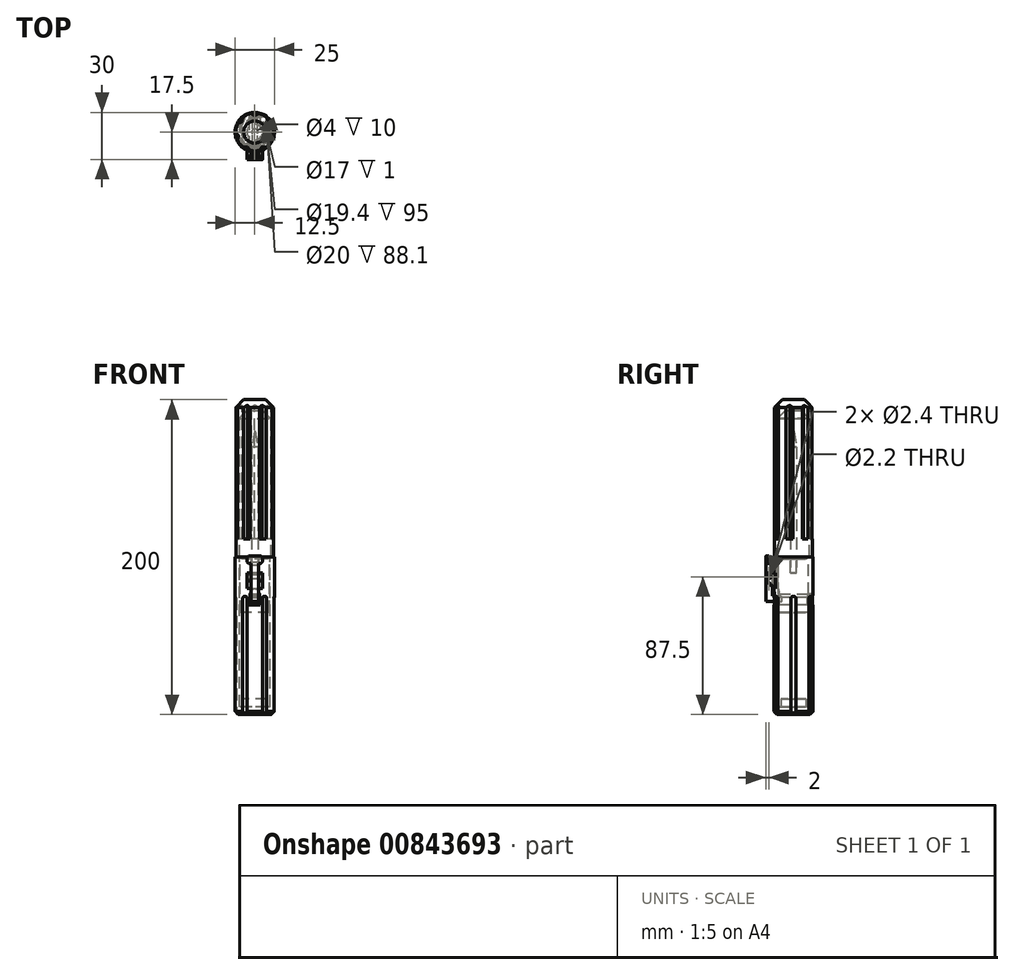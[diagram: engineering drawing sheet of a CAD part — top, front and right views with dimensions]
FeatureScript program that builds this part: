
annotation { "Feature Type Name" : "Feature", "Feature Type Description" : "" }
export const myFeature = defineFeature(function(context is Context, id is Id, definition is map)
    precondition{}
    {
        {
            var Q0;
            Q0=qCreatedBy(makeId("Top.planeOp"),FACE);
            var sketch = newSketch(context, id + "F0", { "sketchPlane" : qUnion([Q0])});
            skCircle(sketch, "E0", {"center": v(0, 0) * mm, "radius": 12.5 * mm});
            skSolve(sketch);
        }
        {
            var Q0;
            Q0=makeQuery(id+"F0.imprint","IMPRINT",FACE,{"disambiguationData":[TD([[makeQuery(id+"F0.imprint","IMPRINT",EDGE,{"derivedFrom":sQuery(id+"F0.wireOp",EDGE,"E0")}),1.0]])]});
            extrude(context, id + "F1", {"entities" : qUnion([Q0]), "depth" : 100 * mm, "offsetDistance" : 25 * mm});
        }
        {
            var Q0;
            Q0=makeQuery(id+"F1.opExtrude","CAP_FACE",FACE,{"disambiguationData":[OSD([sQuery(id+"F0.wireOp",EDGE,"E0")])],"isStart":false});
            var sketch = newSketch(context, id + "F2", { "sketchPlane" : qUnion([Q0])});
            skCircle(sketch, "E1", {"center": v(0, 0) * mm, "radius": 9.7 * mm});
            skSolve(sketch);
        }
        {
            var Q0;
            Q0=qCreatedBy(makeId("Front.planeOp"),FACE);
            var sketch = newSketch(context, id + "F3", { "sketchPlane" : qUnion([Q0])});
            skLineSegment(sketch, "E2.bottom", {"start": v(-5, 85) * mm, "end": v(5, 85) * mm});
            skLineSegment(sketch, "E2.top", {"start": v(-5, 90) * mm, "end": v(5, 90) * mm});
            skLineSegment(sketch, "E2.left", {"start": v(-5, 85) * mm, "end": v(-5, 90) * mm});
            skLineSegment(sketch, "E2.right", {"start": v(5, 85) * mm, "end": v(5, 90) * mm});
            skPoint(sketch, "E2.middle", {"position": v(0, 87.5) * mm});
            skSolve(sketch);
        }
        {
            var Q0;
            Q0 = qSketchRegion(id + "F3", true);
            extrude(context, id + "F4", {"entities" : qUnion([Q0]), "operationType" : NewBodyOperationType.ADD, "depth" : 17.5 * mm, "offsetDistance" : 25 * mm});
        }
        {
            var Q0;
            Q0=makeQuery(id+"F4.boolean.opBoolean","INTERSECT",EDGE,{"derivedFrom":[makeQuery(id+"F1.opExtrude","SWEPT_FACE",FACE,{"disambiguationData":[OSD([sQuery(id+"F0.wireOp",EDGE,"E0")])]}),makeQuery(id+"F4.opExtrude","SWEPT_FACE",FACE,{"disambiguationData":[OSD([sQuery(id+"F3.wireOp",EDGE,"E2.bottom")])]})]});
            chamfer(context, id + "F5", {"entities" : qUnion([Q0]), "width" : 5 * mm, "tangentPropagation" : true});
        }
        {
            var Q0;
            Q0=makeQuery(id+"F4.opExtrude","CAP_FACE",FACE,{"disambiguationData":[OSD([sQuery(id+"F3.wireOp",EDGE,"E2.bottom"),sQuery(id+"F3.wireOp",EDGE,"E2.top"),sQuery(id+"F3.wireOp",EDGE,"E2.left"),sQuery(id+"F3.wireOp",EDGE,"E2.right")])],"isStart":false});
            var sketch = newSketch(context, id + "F6", { "sketchPlane" : qUnion([Q0])});
            skLineSegment(sketch, "E3.bottom", {"start": v(-2.5, 90) * mm, "end": v(2.5, 90) * mm});
            skLineSegment(sketch, "E3.top", {"start": v(-2.5, 80) * mm, "end": v(2.5, 80) * mm});
            skLineSegment(sketch, "E3.left", {"start": v(-2.5, 90) * mm, "end": v(-2.5, 80) * mm});
            skLineSegment(sketch, "E3.right", {"start": v(2.5, 90) * mm, "end": v(2.5, 80) * mm});
            skSolve(sketch);
        }
        {
            var Q0;
            Q0 = qSketchRegion(id + "F6", true);
            extrude(context, id + "F7", {"entities" : qUnion([Q0]), "operationType" : NewBodyOperationType.REMOVE, "oppositeDirection" : true, "depth" : 5 * mm, "offsetDistance" : 25 * mm});
        }
        {
            var Q0;
            {var subQ2=sQuery(id+"F3.wireOp",EDGE,"E2.right");Q0=makeQuery(id+"F4.boolean.opBoolean","SPLIT",FACE,{"disambiguationData":[TD([makeQuery(id+"F1.opExtrude","SWEPT_FACE",FACE,{"disambiguationData":[OSD([sQuery(id+"F0.wireOp",EDGE,"E0")])]})])],"derivedFrom":makeQuery(id+"F4.opExtrude","SWEPT_FACE",FACE,{"disambiguationData":[OSD([subQ2])]})});}
            var sketch = newSketch(context, id + "F8", { "sketchPlane" : qUnion([Q0])});
            skCircle(sketch, "E4", {"center": v(-15.5, 87.5) * mm, "radius": 1.1 * mm});
            skSolve(sketch);
        }
        {
            var Q0;
            Q0 = qSketchRegion(id + "F8", true);
            extrude(context, id + "F9", {"entities" : qUnion([Q0]), "operationType" : NewBodyOperationType.REMOVE, "oppositeDirection" : true, "depth" : 25 * mm, "offsetDistance" : 25 * mm});
        }
        {
            var Q0;
            Q0=makeQuery(id+"F7.boolean.opBoolean","COPY",FACE,{"derivedFrom":makeQuery(id+"F7.opExtrude","CAP_FACE",FACE,{"disambiguationData":[OSD([sQuery(id+"F6.wireOp",EDGE,"E3.bottom"),sQuery(id+"F6.wireOp",EDGE,"E3.top"),sQuery(id+"F6.wireOp",EDGE,"E3.left"),sQuery(id+"F6.wireOp",EDGE,"E3.right")])],"isStart":false})});
            var sketch = newSketch(context, id + "F10", { "sketchPlane" : qUnion([Q0])});
            skLineSegment(sketch, "E5.bottom", {"start": v(-3, 80) * mm, "end": v(3, 80) * mm});
            skLineSegment(sketch, "E5.top", {"start": v(-3, 70) * mm, "end": v(3, 70) * mm});
            skLineSegment(sketch, "E5.left", {"start": v(-3, 80) * mm, "end": v(-3, 70) * mm});
            skLineSegment(sketch, "E5.right", {"start": v(3, 80) * mm, "end": v(3, 70) * mm});
            skSolve(sketch);
        }
        {
            var Q0;
            Q0=makeQuery(id+"F10.imprint","IMPRINT",FACE,{"disambiguationData":[TD([[makeQuery(id+"F10.imprint","IMPRINT",EDGE,{"derivedFrom":sQuery(id+"F10.wireOp",EDGE,"E5.bottom")}),-1.0]])]});
            extrude(context, id + "F11", {"entities" : qUnion([Q0]), "operationType" : NewBodyOperationType.REMOVE, "oppositeDirection" : true, "depth" : 9 * mm, "offsetDistance" : 25 * mm});
        }
        {
            var Q0;
            Q0=makeQuery(id+"F2.imprint","IMPRINT",FACE,{"disambiguationData":[TD([[makeQuery(id+"F2.imprint","IMPRINT",EDGE,{"derivedFrom":sQuery(id+"F2.wireOp",EDGE,"E1")}),1.0]])]});
            extrude(context, id + "F12", {"entities" : qUnion([Q0]), "operationType" : NewBodyOperationType.REMOVE, "oppositeDirection" : true, "depth" : 95 * mm, "offsetDistance" : 25 * mm});
        }
        {
            var Q0;
            Q0=makeQuery(id+"F1.opExtrude","CAP_EDGE",EDGE,{"disambiguationData":[OSD([sQuery(id+"F0.wireOp",EDGE,"E0")])],"isStart":true});
            chamfer(context, id + "F13", {"entities" : qUnion([Q0]), "width" : 2 * mm, "tangentPropagation" : true});
        }
        {
            var Q0;
            Q0=makeQuery(id+"F1.opExtrude","CAP_FACE",FACE,{"disambiguationData":[OSD([sQuery(id+"F0.wireOp",EDGE,"E0")])],"isStart":true});
            var sketch = newSketch(context, id + "F14", { "sketchPlane" : qUnion([Q0])});
            skCircle(sketch, "E6", {"center": v(13.39, 0) * mm, "radius": 1.9 * mm});
            skCircle(sketch, "E7.1.0", {"center": v(6.7, 11.6) * mm, "radius": 1.9 * mm});
            skCircle(sketch, "E7.2.0", {"center": v(-6.7, 11.6) * mm, "radius": 1.9 * mm});
            skCircle(sketch, "E7.3.0", {"center": v(-13.39, 0) * mm, "radius": 1.9 * mm});
            skCircle(sketch, "E7.4.0", {"center": v(-6.7, -11.6) * mm, "radius": 1.9 * mm});
            skCircle(sketch, "E7.5.0", {"center": v(6.7, -11.6) * mm, "radius": 1.9 * mm});
            skPoint(sketch, "E7.center", {"position": v(0, 0) * mm});
            skSolve(sketch);
        }
        {
            var Q0;
            Q0 = qSketchRegion(id + "F14", true);
            extrude(context, id + "F15", {"entities" : qUnion([Q0]), "operationType" : NewBodyOperationType.REMOVE, "oppositeDirection" : true, "depth" : 75 * mm, "offsetDistance" : 25 * mm});
        }
        {
            var Q0;
            Q0=makeQuery(id+"F15.boolean.opBoolean","COPY",EDGE,{"derivedFrom":makeQuery(id+"F15.opExtrude","CAP_EDGE",EDGE,{"disambiguationData":[OSD([sQuery(id+"F14.wireOp",EDGE,"E7.4.0")])],"isStart":false})});
            var Q1;
            Q1=makeQuery(id+"F15.boolean.opBoolean","COPY",EDGE,{"derivedFrom":makeQuery(id+"F15.opExtrude","CAP_EDGE",EDGE,{"disambiguationData":[OSD([sQuery(id+"F14.wireOp",EDGE,"E7.5.0")])],"isStart":false})});
            var Q2;
            Q2=makeQuery(id+"F15.boolean.opBoolean","COPY",EDGE,{"derivedFrom":makeQuery(id+"F15.opExtrude","CAP_EDGE",EDGE,{"disambiguationData":[OSD([sQuery(id+"F14.wireOp",EDGE,"E6")])],"isStart":false})});
            var Q3;
            Q3=makeQuery(id+"F15.boolean.opBoolean","COPY",EDGE,{"derivedFrom":makeQuery(id+"F15.opExtrude","CAP_EDGE",EDGE,{"disambiguationData":[OSD([sQuery(id+"F14.wireOp",EDGE,"E7.1.0")])],"isStart":false})});
            var Q4;
            Q4=makeQuery(id+"F15.boolean.opBoolean","COPY",EDGE,{"derivedFrom":makeQuery(id+"F15.opExtrude","CAP_EDGE",EDGE,{"disambiguationData":[OSD([sQuery(id+"F14.wireOp",EDGE,"E7.2.0")])],"isStart":false})});
            var Q5;
            Q5=makeQuery(id+"F15.boolean.opBoolean","COPY",EDGE,{"derivedFrom":makeQuery(id+"F15.opExtrude","CAP_EDGE",EDGE,{"disambiguationData":[OSD([sQuery(id+"F14.wireOp",EDGE,"E7.3.0")])],"isStart":false})});
            fillet(context, id + "F16", {"entities" : qUnion([Q0, Q1, Q2, Q3, Q4, Q5]), "radius" : 1 * mm, "tangentPropagation" : true, "allowEdgeOverflow" : false});
        }
        {
            var Q0;
            Q0=makeQuery(id+"F11.boolean.opBoolean","COPY",EDGE,{"derivedFrom":makeQuery(id+"F11.opExtrude","SWEPT_EDGE",EDGE,{"disambiguationData":[OSD([sQuery(id+"F10.wireOp",EDGE,"E5.bottom"),sQuery(id+"F10.wireOp",EDGE,"E5.left")])]})});
            var Q1;
            Q1=makeQuery(id+"F11.boolean.opBoolean","COPY",EDGE,{"derivedFrom":makeQuery(id+"F11.opExtrude","SWEPT_EDGE",EDGE,{"disambiguationData":[OSD([sQuery(id+"F10.wireOp",EDGE,"E5.bottom"),sQuery(id+"F10.wireOp",EDGE,"E5.right")])]})});
            fillet(context, id + "F17", {"entities" : qUnion([Q0, Q1]), "radius" : 3 * mm, "tangentPropagation" : true, "allowEdgeOverflow" : false});
        }
        {
            var Q0;
            Q0=makeQuery(id+"F12.boolean.opBoolean","COPY",FACE,{"derivedFrom":makeQuery(id+"F12.opExtrude","CAP_FACE",FACE,{"disambiguationData":[OSD([sQuery(id+"F2.wireOp",EDGE,"E1")])],"isStart":false})});
            var sketch = newSketch(context, id + "F18", { "sketchPlane" : qUnion([Q0])});
            skCircle(sketch, "E8", {"center": v(0, 0) * mm, "radius": 7.9 * mm});
            skSolve(sketch);
        }
        {
            var Q0;
            Q0=makeQuery(id+"F18.imprint","IMPRINT",FACE,{"disambiguationData":[TD([[makeQuery(id+"F18.imprint","IMPRINT",EDGE,{"derivedFrom":sQuery(id+"F18.wireOp",EDGE,"E8")}),1.0]])]});
            extrude(context, id + "F19", {"entities" : qUnion([Q0]), "operationType" : NewBodyOperationType.ADD, "depth" : 5 * mm, "offsetDistance" : 25 * mm});
        }
        {
            var Q0;
            Q0=makeQuery(id+"F7.boolean.opBoolean","COPY",FACE,{"derivedFrom":makeQuery(id+"F7.opExtrude","CAP_FACE",FACE,{"disambiguationData":[OSD([sQuery(id+"F6.wireOp",EDGE,"E3.bottom"),sQuery(id+"F6.wireOp",EDGE,"E3.top"),sQuery(id+"F6.wireOp",EDGE,"E3.left"),sQuery(id+"F6.wireOp",EDGE,"E3.right")])],"isStart":false})});
            var sketch = newSketch(context, id + "F20", { "sketchPlane" : qUnion([Q0])});
            skLineSegment(sketch, "E9.bottom", {"start": v(2.5, 90) * mm, "end": v(-2.5, 90) * mm});
            skLineSegment(sketch, "E9.top", {"start": v(2.5, 101.53) * mm, "end": v(-2.5, 101.53) * mm});
            skLineSegment(sketch, "E9.left", {"start": v(2.5, 90) * mm, "end": v(2.5, 101.53) * mm});
            skLineSegment(sketch, "E9.right", {"start": v(-2.5, 90) * mm, "end": v(-2.5, 101.53) * mm});
            skSolve(sketch);
        }
        {
            var Q0;
            Q0=makeQuery(id+"F20.imprint","IMPRINT",FACE,{"disambiguationData":[TD([[makeQuery(id+"F20.imprint","IMPRINT",EDGE,{"derivedFrom":sQuery(id+"F20.wireOp",EDGE,"E9.top")}),1.0]])]});
            extrude(context, id + "F21", {"entities" : qUnion([Q0]), "operationType" : NewBodyOperationType.REMOVE, "oppositeDirection" : true, "depth" : 2 * mm, "offsetDistance" : 25 * mm});
        }
        {
            var Q0;
            Q0=makeQuery(id+"F1.opExtrude","CAP_FACE",FACE,{"disambiguationData":[OSD([sQuery(id+"F0.wireOp",EDGE,"E0")])],"isStart":false});
            var sketch = newSketch(context, id + "F22", { "sketchPlane" : qUnion([Q0])});
            skCircle(sketch, "E10", {"center": v(0, 0) * mm, "radius": 9.5 * mm});
            skSolve(sketch);
        }
        {
            var Q0;
            Q0=makeQuery(id+"F22.imprint","IMPRINT",FACE,{"disambiguationData":[TD([[makeQuery(id+"F22.imprint","IMPRINT",EDGE,{"derivedFrom":sQuery(id+"F22.wireOp",EDGE,"E10")}),1.0]])]});
            extrude(context, id + "F23", {"entities" : qUnion([Q0]), "oppositeDirection" : true, "depth" : 35 * mm, "offsetDistance" : 25 * mm});
        }
        {
            var Q0;
            Q0=makeQuery(id+"F7.boolean.opBoolean","COPY",FACE,{"derivedFrom":makeQuery(id+"F7.opExtrude","CAP_FACE",FACE,{"disambiguationData":[OSD([sQuery(id+"F6.wireOp",EDGE,"E3.bottom"),sQuery(id+"F6.wireOp",EDGE,"E3.top"),sQuery(id+"F6.wireOp",EDGE,"E3.left"),sQuery(id+"F6.wireOp",EDGE,"E3.right")])],"isStart":false})});
            var sketch = newSketch(context, id + "F24", { "sketchPlane" : qUnion([Q0])});
            skLineSegment(sketch, "E11.bottom", {"start": v(-3.5, 69.5) * mm, "end": v(3.5, 69.5) * mm});
            skLineSegment(sketch, "E11.top", {"start": v(-3.5, 76.5) * mm, "end": v(3.5, 76.5) * mm});
            skLineSegment(sketch, "E11.left", {"start": v(-3.5, 69.5) * mm, "end": v(-3.5, 76.5) * mm});
            skLineSegment(sketch, "E11.right", {"start": v(3.5, 69.5) * mm, "end": v(3.5, 76.5) * mm});
            skSolve(sketch);
        }
        {
            var Q0;
            Q0=makeQuery(id+"F24.imprint","IMPRINT",FACE,{"disambiguationData":[TD([[makeQuery(id+"F24.imprint","IMPRINT",EDGE,{"derivedFrom":sQuery(id+"F24.wireOp",EDGE,"E11.bottom")}),1.0]])]});
            extrude(context, id + "F25", {"entities" : qUnion([Q0]), "operationType" : NewBodyOperationType.REMOVE, "oppositeDirection" : true, "depth" : 25 * mm, "offsetDistance" : 25 * mm});
        }
        {
            var Q0;
            Q0=makeQuery(id+"F25.boolean.opBoolean","COPY",EDGE,{"derivedFrom":makeQuery(id+"F25.opExtrude","SWEPT_EDGE",EDGE,{"disambiguationData":[OSD([sQuery(id+"F24.wireOp",EDGE,"E11.top"),sQuery(id+"F24.wireOp",EDGE,"E11.left")])]})});
            var Q1;
            Q1=makeQuery(id+"F25.boolean.opBoolean","COPY",EDGE,{"derivedFrom":makeQuery(id+"F25.opExtrude","SWEPT_EDGE",EDGE,{"disambiguationData":[OSD([sQuery(id+"F24.wireOp",EDGE,"E11.top"),sQuery(id+"F24.wireOp",EDGE,"E11.right")])]})});
            chamfer(context, id + "F26", {"entities" : qUnion([Q0, Q1]), "width" : 2 * mm, "tangentPropagation" : true});
        }
        {
            var Q0;
            Q0=makeQuery(id+"F23.opExtrude","CAP_FACE",FACE,{"disambiguationData":[OSD([sQuery(id+"F22.wireOp",EDGE,"E10")])],"isStart":true});
            var sketch = newSketch(context, id + "F27", { "sketchPlane" : qUnion([Q0])});
            skCircle(sketch, "E12", {"center": v(0, 0) * mm, "radius": 2 * mm});
            skSolve(sketch);
        }
        {
            var Q0;
            Q0=makeQuery(id+"F27.imprint","IMPRINT",FACE,{"disambiguationData":[TD([[makeQuery(id+"F27.imprint","IMPRINT",EDGE,{"derivedFrom":sQuery(id+"F27.wireOp",EDGE,"E12")}),1.0]])]});
            extrude(context, id + "F28", {"entities" : qUnion([Q0]), "operationType" : NewBodyOperationType.REMOVE, "oppositeDirection" : true, "depth" : 10 * mm, "offsetDistance" : 25 * mm});
        }
        {
            var Q0;
            Q0=makeQuery(id+"F23.opExtrude","CAP_FACE",FACE,{"disambiguationData":[OSD([sQuery(id+"F22.wireOp",EDGE,"E10")])],"isStart":true});
            var sketch = newSketch(context, id + "F29", { "sketchPlane" : qUnion([Q0])});
            skCircle(sketch, "E13", {"center": v(0, 0) * mm, "radius": 7.5 * mm});
            skCircle(sketch, "E14", {"center": v(0, 0) * mm, "radius": 8.5 * mm});
            skSolve(sketch);
        }
        {
            var Q0;
            Q0=makeQuery(id+"F29.imprint","IMPRINT",FACE,{"disambiguationData":[TD([[makeQuery(id+"F29.imprint","IMPRINT",EDGE,{"derivedFrom":sQuery(id+"F29.wireOp",EDGE,"E13")}),-1.0]])]});
            extrude(context, id + "F30", {"entities" : qUnion([Q0]), "operationType" : NewBodyOperationType.REMOVE, "oppositeDirection" : true, "depth" : 1 * mm, "offsetDistance" : 25 * mm});
        }
        {
            var Q0;
            Q0=makeQuery(id+"F7.boolean.opBoolean","COPY",FACE,{"derivedFrom":makeQuery(id+"F7.opExtrude","SWEPT_FACE",FACE,{"disambiguationData":[OSD([sQuery(id+"F6.wireOp",EDGE,"E3.right")])]})});
            var sketch = newSketch(context, id + "F31", { "sketchPlane" : qUnion([Q0])});
            skLineSegment(sketch, "E15.bottom", {"start": v(17.43, 72) * mm, "end": v(13.43, 72) * mm});
            skLineSegment(sketch, "E15.top", {"start": v(17.43, 100) * mm, "end": v(13.43, 100) * mm});
            skLineSegment(sketch, "E15.left", {"start": v(17.43, 72) * mm, "end": v(17.43, 100) * mm});
            skLineSegment(sketch, "E15.right", {"start": v(13.43, 72) * mm, "end": v(13.43, 100) * mm});
            skSolve(sketch);
        }
        {
            var Q0;
            Q0 = qSketchRegion(id + "F31", true);
            extrude(context, id + "F32", {"entities" : qUnion([Q0]), "depth" : 4.8 * mm, "offsetDistance" : 25 * mm});
        }
        {
            var Q0;
            Q0=makeQuery(id+"F32.opExtrude","SWEPT_EDGE",EDGE,{"disambiguationData":[OSD([sQuery(id+"F31.wireOp",EDGE,"E15.top"),sQuery(id+"F31.wireOp",EDGE,"E15.right")])]});
            chamfer(context, id + "F33", {"entities" : qUnion([Q0]), "width" : 5 * mm, "tangentPropagation" : true});
        }
        {
            var Q0;
            Q0=makeQuery(id+"F32.opExtrude","SWEPT_FACE",FACE,{"disambiguationData":[OSD([sQuery(id+"F31.wireOp",EDGE,"E15.left")])]});
            var sketch = newSketch(context, id + "F34", { "sketchPlane" : qUnion([Q0])});
            skLineSegment(sketch, "E16.bottom", {"start": v(5, 100.9) * mm, "end": v(-5, 100.9) * mm});
            skLineSegment(sketch, "E16.top", {"start": v(5, 95.9) * mm, "end": v(-5, 95.9) * mm});
            skLineSegment(sketch, "E16.left", {"start": v(5, 100.9) * mm, "end": v(5, 95.9) * mm});
            skLineSegment(sketch, "E16.right", {"start": v(-5, 100.9) * mm, "end": v(-5, 95.9) * mm});
            skPoint(sketch, "E16.middle", {"position": v(0, 97.45) * mm});
            skSolve(sketch);
        }
        {
            var Q0;
            Q0 = qSketchRegion(id + "F34", true);
            extrude(context, id + "F35", {"entities" : qUnion([Q0]), "operationType" : NewBodyOperationType.ADD, "oppositeDirection" : true, "depth" : 2 * mm, "offsetDistance" : 25 * mm});
        }
        {
            var Q0;
            Q0=makeQuery(id+"F35.opExtrude","SWEPT_EDGE",EDGE,{"disambiguationData":[OSD([sQuery(id+"F34.wireOp",EDGE,"E16.top"),sQuery(id+"F34.wireOp",EDGE,"E16.right")])]});
            var Q1;
            Q1=makeQuery(id+"F35.opExtrude","SWEPT_EDGE",EDGE,{"disambiguationData":[OSD([sQuery(id+"F34.wireOp",EDGE,"E16.bottom"),sQuery(id+"F34.wireOp",EDGE,"E16.right")])]});
            var Q2;
            Q2=makeQuery(id+"F35.opExtrude","SWEPT_EDGE",EDGE,{"disambiguationData":[OSD([sQuery(id+"F34.wireOp",EDGE,"E16.top"),sQuery(id+"F34.wireOp",EDGE,"E16.left")])]});
            var Q3;
            Q3=makeQuery(id+"F35.opExtrude","SWEPT_EDGE",EDGE,{"disambiguationData":[OSD([sQuery(id+"F34.wireOp",EDGE,"E16.bottom"),sQuery(id+"F34.wireOp",EDGE,"E16.left")])]});
            fillet(context, id + "F36", {"entities" : qUnion([Q0, Q1, Q2, Q3]), "radius" : 2 * mm, "tangentPropagation" : true, "allowEdgeOverflow" : false});
        }
        {
            var Q0;
            Q0=makeQuery(id+"F32.opExtrude","CAP_FACE",FACE,{"disambiguationData":[OSD([sQuery(id+"F31.wireOp",EDGE,"E15.bottom"),sQuery(id+"F31.wireOp",EDGE,"E15.top"),sQuery(id+"F31.wireOp",EDGE,"E15.left"),sQuery(id+"F31.wireOp",EDGE,"E15.right")])],"isStart":false});
            var sketch = newSketch(context, id + "F37", { "sketchPlane" : qUnion([Q0])});
            skCircle(sketch, "E17", {"center": v(15.5, 87.5) * mm, "radius": 1.2 * mm});
            skSolve(sketch);
        }
        {
            var Q0;
            Q0=makeQuery(id+"F37.imprint","IMPRINT",FACE,{"disambiguationData":[TD([[makeQuery(id+"F37.imprint","IMPRINT",EDGE,{"derivedFrom":sQuery(id+"F37.wireOp",EDGE,"E17")}),1.0]])]});
            extrude(context, id + "F38", {"entities" : qUnion([Q0]), "operationType" : NewBodyOperationType.REMOVE, "oppositeDirection" : true, "depth" : 25 * mm, "offsetDistance" : 25 * mm});
        }
        {
            var Q0;
            Q0=makeQuery(id+"F32.opExtrude","SWEPT_FACE",FACE,{"disambiguationData":[OSD([sQuery(id+"F31.wireOp",EDGE,"E15.right")])]});
            var sketch = newSketch(context, id + "F39", { "sketchPlane" : qUnion([Q0])});
            skLineSegment(sketch, "E18.bottom", {"start": v(-2.5, 72) * mm, "end": v(2.3, 72) * mm});
            skLineSegment(sketch, "E18.top", {"start": v(-2.5, 75.3) * mm, "end": v(2.3, 75.3) * mm});
            skLineSegment(sketch, "E18.left", {"start": v(-2.5, 72) * mm, "end": v(-2.5, 75.3) * mm});
            skLineSegment(sketch, "E18.right", {"start": v(2.3, 72) * mm, "end": v(2.3, 75.3) * mm});
            skSolve(sketch);
        }
        {
            var Q0;
            Q0=makeQuery(id+"F39.imprint","IMPRINT",FACE,{"disambiguationData":[TD([[makeQuery(id+"F39.imprint","IMPRINT",EDGE,{"derivedFrom":sQuery(id+"F39.wireOp",EDGE,"E18.bottom")}),-1.0]])]});
            extrude(context, id + "F40", {"entities" : qUnion([Q0]), "operationType" : NewBodyOperationType.ADD, "depth" : 6 * mm, "offsetDistance" : 25 * mm});
        }
        {
            var Q0;
            Q0=makeQuery(id+"F40.opExtrude","CAP_EDGE",EDGE,{"disambiguationData":[OSD([sQuery(id+"F39.wireOp",EDGE,"E18.top")])],"isStart":false});
            chamfer(context, id + "F41", {"entities" : qUnion([Q0]), "width" : 1 * mm, "tangentPropagation" : true});
        }
        {
            var Q0;
            Q0=makeQuery(id+"F1.opExtrude","CAP_FACE",FACE,{"disambiguationData":[OSD([sQuery(id+"F0.wireOp",EDGE,"E0")])],"isStart":false});
            var sketch = newSketch(context, id + "F42", { "sketchPlane" : qUnion([Q0])});
            skCircle(sketch, "E19", {"center": v(0, 0) * mm, "radius": 12 * mm});
            skSolve(sketch);
        }
        {
            var Q0;
            Q0 = qSketchRegion(id + "F42", true);
            extrude(context, id + "F43", {"entities" : qUnion([Q0]), "depth" : 100 * mm, "offsetDistance" : 25 * mm});
        }
        {
            var Q0;
            Q0=makeQuery(id+"F43.opExtrude","CAP_EDGE",EDGE,{"disambiguationData":[OSD([sQuery(id+"F42.wireOp",EDGE,"E19")])],"isStart":false});
            chamfer(context, id + "F44", {"entities" : qUnion([Q0]), "width" : 5 * mm, "tangentPropagation" : true});
        }
        {
            var Q0;
            Q0=makeQuery(id+"F43.opExtrude","CAP_FACE",FACE,{"disambiguationData":[OSD([sQuery(id+"F42.wireOp",EDGE,"E19")])],"isStart":true});
            var sketch = newSketch(context, id + "F45", { "sketchPlane" : qUnion([Q0])});
            skCircle(sketch, "E20", {"center": v(0, 0) * mm, "radius": 10 * mm});
            skSolve(sketch);
        }
        {
            var Q0;
            Q0=makeQuery(id+"F45.imprint","IMPRINT",FACE,{"disambiguationData":[TD([[makeQuery(id+"F45.imprint","IMPRINT",EDGE,{"derivedFrom":sQuery(id+"F45.wireOp",EDGE,"E20")}),1.0]])]});
            extrude(context, id + "F46", {"entities" : qUnion([Q0]), "operationType" : NewBodyOperationType.REMOVE, "oppositeDirection" : true, "depth" : 93.1 * mm, "offsetDistance" : 25 * mm});
        }
        {
            var Q0;
            Q0=makeQuery(id+"F46.boolean.opBoolean","COPY",EDGE,{"derivedFrom":makeQuery(id+"F46.opExtrude","CAP_EDGE",EDGE,{"disambiguationData":[OSD([sQuery(id+"F45.wireOp",EDGE,"E20")])],"isStart":false})});
            chamfer(context, id + "F47", {"entities" : qUnion([Q0]), "width" : 5 * mm, "tangentPropagation" : true});
        }
        {
            var Q0;
            Q0=makeQuery(id+"F43.opExtrude","CAP_FACE",FACE,{"disambiguationData":[OSD([sQuery(id+"F42.wireOp",EDGE,"E19")])],"isStart":false});
            var sketch = newSketch(context, id + "F48", { "sketchPlane" : qUnion([Q0])});
            skCircle(sketch, "E21.cCircle", {"center": v(0, 13.62) * mm, "radius": 2.72 * mm, "construction": true});
            skLineSegment(sketch, "E21.0", {"start": v(-0.02, 16.77) * mm, "end": v(2.71, 15.21) * mm});
            skLineSegment(sketch, "E21.1", {"start": v(2.71, 15.21) * mm, "end": v(2.74, 12.07) * mm});
            skLineSegment(sketch, "E21.2", {"start": v(2.74, 12.07) * mm, "end": v(0.02, 10.48) * mm});
            skLineSegment(sketch, "E21.3", {"start": v(0.02, 10.48) * mm, "end": v(-2.71, 12.03) * mm});
            skLineSegment(sketch, "E21.4", {"start": v(-2.71, 12.03) * mm, "end": v(-2.74, 15.18) * mm});
            skLineSegment(sketch, "E21.5", {"start": v(-2.74, 15.18) * mm, "end": v(-0.02, 16.77) * mm});
            skPoint(sketch, "E21.0.midPoint", {"position": v(1.35, 16) * mm});
            skLineSegment(sketch, "E22.1.0", {"start": v(-10.2, 11.6) * mm, "end": v(-7.73, 9.66) * mm});
            skLineSegment(sketch, "E22.1.1", {"start": v(-7.73, 9.66) * mm, "end": v(-8.18, 6.55) * mm});
            skLineSegment(sketch, "E22.1.2", {"start": v(-8.18, 6.55) * mm, "end": v(-11.1, 5.38) * mm});
            skLineSegment(sketch, "E22.1.3", {"start": v(-11.1, 5.38) * mm, "end": v(-13.57, 7.32) * mm});
            skLineSegment(sketch, "E22.1.4", {"start": v(-13.57, 7.32) * mm, "end": v(-13.12, 10.44) * mm});
            skLineSegment(sketch, "E22.1.5", {"start": v(-13.12, 10.44) * mm, "end": v(-10.2, 11.6) * mm});
            skLineSegment(sketch, "E22.2.0", {"start": v(-15.44, -0.74) * mm, "end": v(-12.38, -0.02) * mm});
            skLineSegment(sketch, "E22.2.1", {"start": v(-12.38, -0.02) * mm, "end": v(-10.22, -2.3) * mm});
            skLineSegment(sketch, "E22.2.2", {"start": v(-10.22, -2.3) * mm, "end": v(-11.13, -5.32) * mm});
            skLineSegment(sketch, "E22.2.3", {"start": v(-11.13, -5.32) * mm, "end": v(-14.19, -6.04) * mm});
            skLineSegment(sketch, "E22.2.4", {"start": v(-14.19, -6.04) * mm, "end": v(-16.34, -3.75) * mm});
            skLineSegment(sketch, "E22.2.5", {"start": v(-16.34, -3.75) * mm, "end": v(-15.44, -0.74) * mm});
            skLineSegment(sketch, "E22.3.0", {"start": v(-9.05, -12.53) * mm, "end": v(-7.7, -9.69) * mm});
            skLineSegment(sketch, "E22.3.1", {"start": v(-7.7, -9.69) * mm, "end": v(-4.57, -9.43) * mm});
            skLineSegment(sketch, "E22.3.2", {"start": v(-4.57, -9.43) * mm, "end": v(-2.78, -12.02) * mm});
            skLineSegment(sketch, "E22.3.3", {"start": v(-2.78, -12.02) * mm, "end": v(-4.12, -14.86) * mm});
            skLineSegment(sketch, "E22.3.4", {"start": v(-4.12, -14.86) * mm, "end": v(-7.26, -15.12) * mm});
            skLineSegment(sketch, "E22.3.5", {"start": v(-7.26, -15.12) * mm, "end": v(-9.05, -12.53) * mm});
            skLineSegment(sketch, "E22.4.0", {"start": v(4.16, -14.89) * mm, "end": v(2.77, -12.06) * mm});
            skLineSegment(sketch, "E22.4.1", {"start": v(2.77, -12.06) * mm, "end": v(4.53, -9.45) * mm});
            skLineSegment(sketch, "E22.4.2", {"start": v(4.53, -9.45) * mm, "end": v(7.66, -9.66) * mm});
            skLineSegment(sketch, "E22.4.3", {"start": v(7.66, -9.66) * mm, "end": v(9.05, -12.49) * mm});
            skLineSegment(sketch, "E22.4.4", {"start": v(9.05, -12.49) * mm, "end": v(7.3, -15.1) * mm});
            skLineSegment(sketch, "E22.4.5", {"start": v(7.3, -15.1) * mm, "end": v(4.16, -14.89) * mm});
            skLineSegment(sketch, "E22.5.0", {"start": v(14.23, -6.03) * mm, "end": v(11.16, -5.35) * mm});
            skLineSegment(sketch, "E22.5.1", {"start": v(11.16, -5.35) * mm, "end": v(10.2, -2.35) * mm});
            skLineSegment(sketch, "E22.5.2", {"start": v(10.2, -2.35) * mm, "end": v(12.33, -0.03) * mm});
            skLineSegment(sketch, "E22.5.3", {"start": v(12.33, -0.03) * mm, "end": v(15.4, -0.71) * mm});
            skLineSegment(sketch, "E22.5.4", {"start": v(15.4, -0.71) * mm, "end": v(16.35, -3.7) * mm});
            skLineSegment(sketch, "E22.5.5", {"start": v(16.35, -3.7) * mm, "end": v(14.23, -6.03) * mm});
            skLineSegment(sketch, "E22.6.0", {"start": v(13.59, 7.36) * mm, "end": v(11.14, 5.39) * mm});
            skLineSegment(sketch, "E22.6.1", {"start": v(11.14, 5.39) * mm, "end": v(8.2, 6.52) * mm});
            skLineSegment(sketch, "E22.6.2", {"start": v(8.2, 6.52) * mm, "end": v(7.71, 9.62) * mm});
            skLineSegment(sketch, "E22.6.3", {"start": v(7.71, 9.62) * mm, "end": v(10.16, 11.6) * mm});
            skLineSegment(sketch, "E22.6.4", {"start": v(10.16, 11.6) * mm, "end": v(13.1, 10.47) * mm});
            skLineSegment(sketch, "E22.6.5", {"start": v(13.1, 10.47) * mm, "end": v(13.59, 7.36) * mm});
            skPoint(sketch, "E22.center", {"position": v(0, 0) * mm});
            skSolve(sketch);
        }
        {
            var Q0;
            Q0 = qSketchRegion(id + "F48", true);
            extrude(context, id + "F49", {"entities" : qUnion([Q0]), "operationType" : NewBodyOperationType.REMOVE, "oppositeDirection" : true, "depth" : 88.3 * mm, "offsetDistance" : 25 * mm});
        }
        {
            var Q0;
            Q0=makeQuery(id+"F28.boolean.opBoolean","COPY",FACE,{"derivedFrom":makeQuery(id+"F28.opExtrude","CAP_FACE",FACE,{"disambiguationData":[OSD([sQuery(id+"F27.wireOp",EDGE,"E12")])],"isStart":false})});
            var sketch = newSketch(context, id + "F50", { "sketchPlane" : qUnion([Q0])});
            skCircle(sketch, "E23", {"center": v(0, 0) * mm, "radius": 1.98 * mm});
            skSolve(sketch);
        }
        {
            var Q0;
            Q0=makeQuery(id+"F50.imprint","IMPRINT",FACE,{"disambiguationData":[TD([[makeQuery(id+"F50.imprint","IMPRINT",EDGE,{"derivedFrom":sQuery(id+"F50.wireOp",EDGE,"E23")}),1.0]])]});
            extrude(context, id + "F51", {"entities" : qUnion([Q0]), "depth" : 90 * mm, "offsetDistance" : 25 * mm});
        }
        {
            var Q0;
            Q0=makeQuery(id+"F51.opExtrude","CAP_EDGE",EDGE,{"disambiguationData":[OSD([sQuery(id+"F50.wireOp",EDGE,"E23")])],"isStart":false});
            chamfer(context, id + "F52", {"entities" : qUnion([Q0]), "chamferType" : ChamferType.OFFSET_ANGLE, "width" : 10 * mm, "oppositeDirection" : true, "angle" : 10 * degree});
        }
    });
